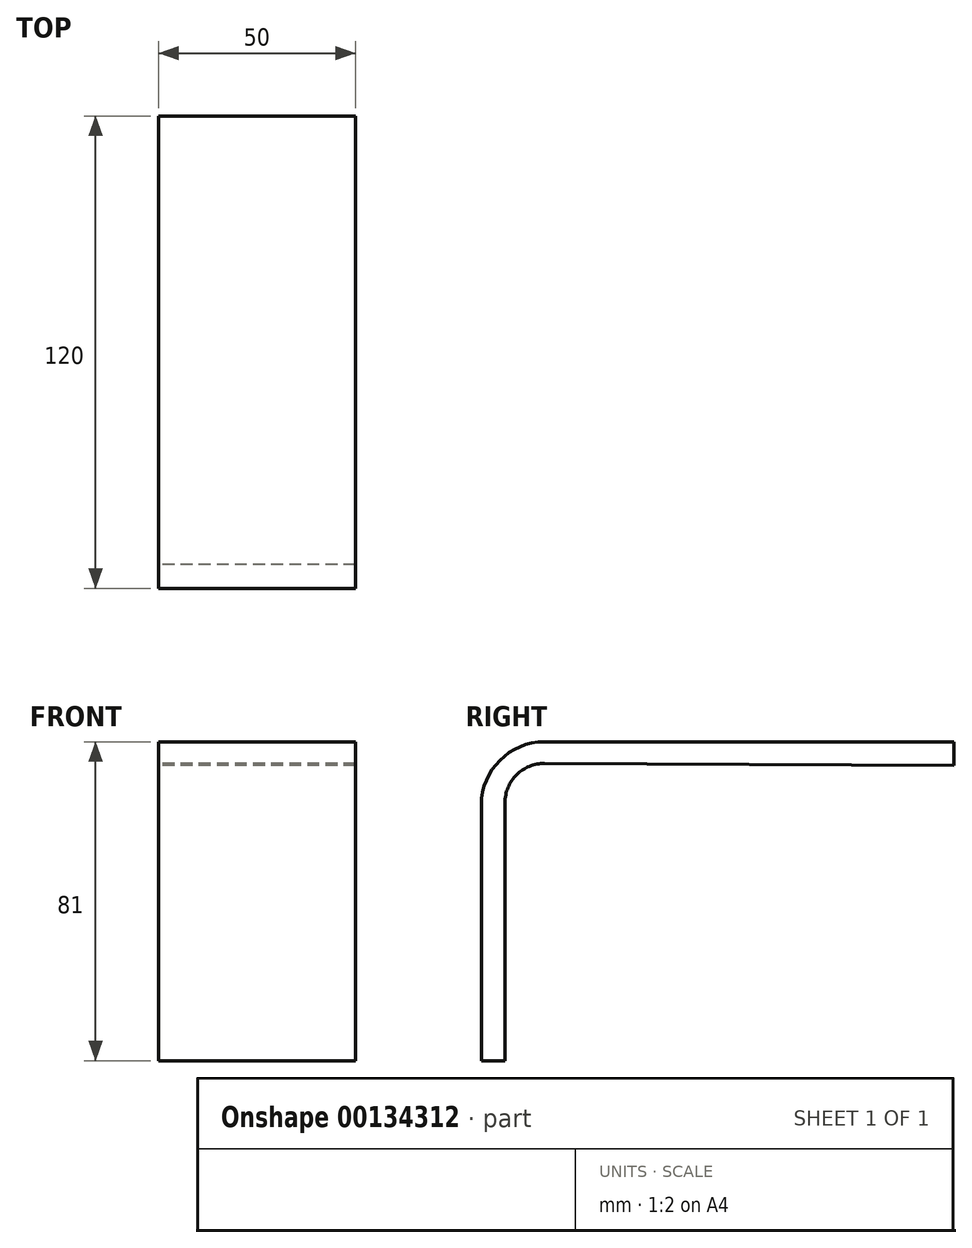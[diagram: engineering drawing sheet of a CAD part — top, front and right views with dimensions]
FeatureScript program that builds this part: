
annotation { "Feature Type Name" : "Feature", "Feature Type Description" : "" }
export const myFeature = defineFeature(function(context is Context, id is Id, definition is map)
    precondition{}
    {
        {
            var Q0;
            Q0=qCreatedBy(makeId("Right.planeOp"),FACE);
            var sketch = newSketch(context, id + "F0", { "sketchPlane" : qUnion([Q0])});
            skLineSegment(sketch, "E0", {"start": v(-38.4, 34.03) * mm, "end": v(65.6, 34.03) * mm});
            skLineSegment(sketch, "E1", {"start": v(-54.4, 18.03) * mm, "end": v(-54.4, -46.97) * mm});
            skLineSegment(sketch, "E2", {"start": v(-54.4, -46.97) * mm, "end": v(-48.4, -46.97) * mm});
            skLineSegment(sketch, "E3", {"start": v(-48.4, -46.97) * mm, "end": v(-48.4, 18.58) * mm});
            skLineSegment(sketch, "E4", {"start": v(65.6, 34.03) * mm, "end": v(65.6, 28.03) * mm});
            skLineSegment(sketch, "E5", {"start": v(65.6, 28.03) * mm, "end": v(-38.35, 28.58) * mm});
            skPoint(sketch, "E6.visualSharp", {"position": v(-48.4, 28.63) * mm});
            skArc(sketch, "E6.filletArc", {"start": v(-38.35, 28.58) * mm, "mid": v(-45.46, 25.67) * mm, "end": v(-48.4, 18.58) * mm});
            skArc(sketch, "E7.filletArc", {"start": v(-38.4, 34.03) * mm, "mid": v(-49.72, 29.35) * mm, "end": v(-54.4, 18.03) * mm});
            skSolve(sketch);
        }
        {
            var Q0;
            Q0=makeQuery(id+"F0.imprint","IMPRINT",FACE,{"disambiguationData":[TD([[makeQuery(id+"F0.imprint","IMPRINT",EDGE,{"derivedFrom":sQuery(id+"F0.wireOp",EDGE,"E0")}),-1.0]])]});
            extrude(context, id + "F1", {"entities" : qUnion([Q0]), "depth" : 50 * mm});
        }
    });
